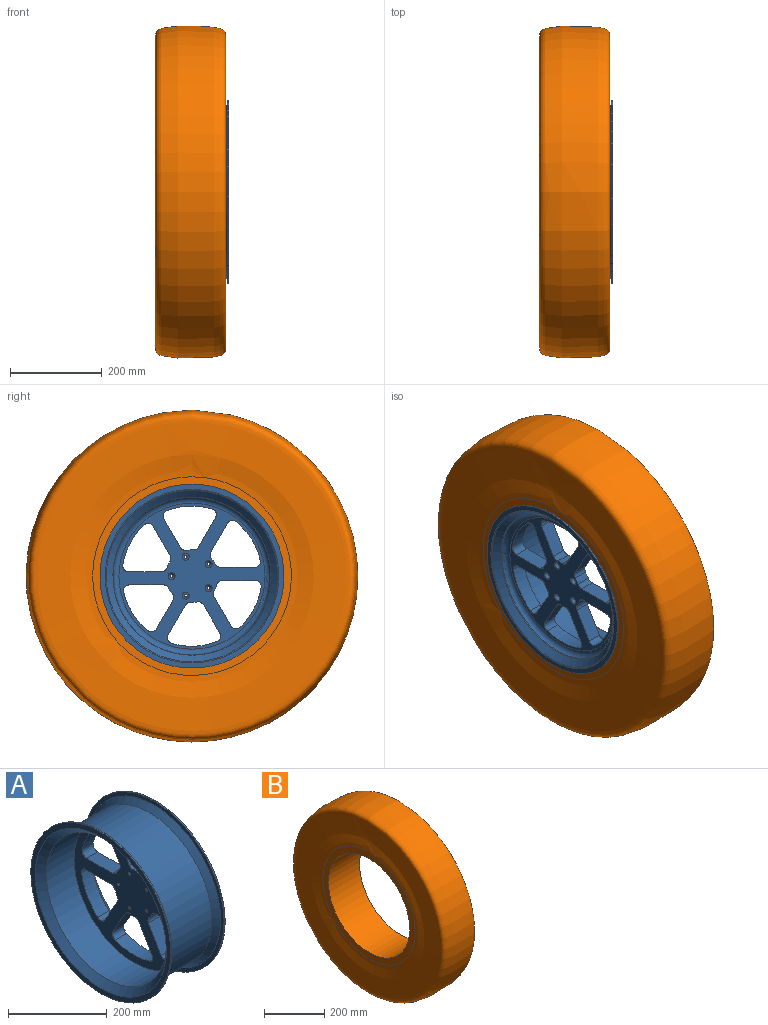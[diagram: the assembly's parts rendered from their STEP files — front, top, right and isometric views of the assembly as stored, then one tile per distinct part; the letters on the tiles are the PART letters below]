
ASSEMBLY  parts=2 mates=1
PART A: 80 faces, bbox 155.6x413.2x413.2 mm
  f0: plane 342.9x342.9mm, normal (-1,0,0), area 46675.4mm2, adj f7,f17,f18,f19,f20,f21,f22,f23
  f1: plane 317.61x317.61mm, normal (1,0,0), area 32801.7mm2, adj f16,f17,f18,f19,f20,f21,f22,f23
  f2: cone r=177.8mm half-angle=45deg, axis (-1,0,0), area 20781.2mm2, adj f3,f13
  f3: plane 400.05x400.05mm, normal (1,0,0), area 11685.9mm2, adj f2,f4
  f4: cylinder r=200.03mm len=400.05mm, axis (1,0,0), area 3990.3mm2, adj f3,f5
  f5: plane 400.05x400.05mm, normal (-1,0,0), area 15454.6mm2, adj f4,f6
  f6: cone r=171.45mm half-angle=45deg, axis (-1,0,0), area 25304.7mm2, adj f5,f7
  f7: cylinder r=171.45mm len=342.9mm, axis (1,0,0), area 85506.9mm2, adj f0,f6
  f8: cone r=187.32mm half-angle=45deg, axis (1,0,0), area 22340mm2, adj f14,f15
  f9: plane 400.05x400.05mm, normal (1,0,0), area 13901.2mm2, adj f10,f15
  f10: cylinder r=200.03mm len=400.05mm, axis (1,0,0), area 3990.3mm2, adj f9,f11
  f11: plane 400.05x400.05mm, normal (-1,0,0), area 11685.9mm2, adj f10,f12
  f12: cone r=177.8mm half-angle=45deg, axis (1,0,0), area 20781.2mm2, adj f11,f13
  f13: cylinder r=177.8mm len=355.6mm, axis (1,0,0), area 138331.1mm2, adj f2,f12
  f14: torus R=174.62mm, axis (-1,0,0), area 2407.6mm2, adj f8,f16
  f15: torus R=188.64mm, axis (-1,0,0), area 2937.1mm2, adj f8,f9
  f16: torus R=158.8mm, axis (-1,0,0), area 19783.7mm2, adj f1,f14
  f17: plane 62.09x35.85mm, normal (0,0.87,-0.5), area 2276.5mm2, adj f0,f1,f21,f24
  f18: cylinder r=57.15mm len=31.75mm, axis (1,0,0), area 456.4mm2, adj f0,f1,f21,f22
  f19: plane 73.83x31.75mm, normal (0,0,1), area 2344mm2, adj f0,f1,f22,f23
  f20: cylinder r=152.4mm len=83.54mm, axis (1,0,0), area 3184.6mm2, adj f0,f1,f23,f24
  f21: cylinder r=12.7mm len=31.75mm, axis (1,0,0), area 502.8mm2, adj f0,f1,f17,f18
  f22: cylinder r=12.7mm len=31.75mm, axis (1,0,0), area 443.1mm2, adj f0,f1,f18,f19
  f23: cylinder r=12.7mm len=31.75mm, axis (1,0,0), area 725.8mm2, adj f0,f1,f19,f20
  f24: cylinder r=12.7mm len=31.75mm, axis (1,0,0), area 697.8mm2, adj f0,f1,f17,f20
  f25: plane 71.7x31.75mm, normal (0,0,-1), area 2276.5mm2, adj f0,f1,f29,f32
  f26: cylinder r=57.15mm len=31.75mm, axis (1,0,0), area 456.4mm2, adj f0,f1,f29,f30
  f27: plane 63.94x36.91mm, normal (0,0.87,0.5), area 2344mm2, adj f0,f1,f30,f31
  f28: cylinder r=152.4mm len=86.97mm, axis (1,0,0), area 3184.6mm2, adj f0,f1,f31,f32
  f29: cylinder r=12.7mm len=31.75mm, axis (1,0,0), area 502.8mm2, adj f0,f1,f25,f26
  f30: cylinder r=12.7mm len=31.75mm, axis (1,0,0), area 443.1mm2, adj f0,f1,f26,f27
  f31: cylinder r=12.7mm len=31.75mm, axis (1,0,0), area 725.8mm2, adj f0,f1,f27,f28
  f32: cylinder r=12.7mm len=31.75mm, axis (1,0,0), area 697.8mm2, adj f0,f1,f25,f28
  f33: plane 62.09x35.85mm, normal (0,-0.87,-0.5), area 2276.5mm2, adj f0,f1,f37,f40
  f34: cylinder r=57.15mm len=31.75mm, axis (1,0,0), area 456.4mm2, adj f0,f1,f37,f38
  f35: plane 63.94x36.91mm, normal (0,0.87,-0.5), area 2344mm2, adj f0,f1,f38,f39
  f36: cylinder r=152.4mm len=98.44mm, axis (1,0,0), area 3184.6mm2, adj f0,f1,f39,f40
  f37: cylinder r=12.7mm len=31.75mm, axis (1,0,0), area 502.8mm2, adj f0,f1,f33,f34
  f38: cylinder r=12.7mm len=31.75mm, axis (1,0,0), area 443.1mm2, adj f0,f1,f34,f35
  f39: cylinder r=12.7mm len=31.75mm, axis (1,0,0), area 725.8mm2, adj f0,f1,f35,f36
  f40: cylinder r=12.7mm len=31.75mm, axis (1,0,0), area 697.8mm2, adj f0,f1,f33,f36
  f41: plane 62.09x35.85mm, normal (0,-0.87,0.5), area 2276.5mm2, adj f0,f1,f45,f48
  f42: cylinder r=57.15mm len=31.75mm, axis (1,0,0), area 456.4mm2, adj f0,f1,f45,f46
  f43: plane 73.83x31.75mm, normal (0,0,-1), area 2344mm2, adj f0,f1,f46,f47
  f44: cylinder r=152.4mm len=83.54mm, axis (1,0,0), area 3184.6mm2, adj f0,f1,f47,f48
  f45: cylinder r=12.7mm len=31.75mm, axis (1,0,0), area 502.8mm2, adj f0,f1,f41,f42
  f46: cylinder r=12.7mm len=31.75mm, axis (1,0,0), area 443.1mm2, adj f0,f1,f42,f43
  f47: cylinder r=12.7mm len=31.75mm, axis (1,0,0), area 725.8mm2, adj f0,f1,f43,f44
  f48: cylinder r=12.7mm len=31.75mm, axis (1,0,0), area 697.8mm2, adj f0,f1,f41,f44
  f49: plane 71.7x31.75mm, normal (0,0,1), area 2276.5mm2, adj f0,f1,f53,f56
  f50: cylinder r=57.15mm len=31.75mm, axis (1,0,0), area 456.4mm2, adj f0,f1,f53,f54
  f51: plane 63.94x36.91mm, normal (0,-0.87,-0.5), area 2344mm2, adj f0,f1,f54,f55
  f52: cylinder r=152.4mm len=86.97mm, axis (1,0,0), area 3184.6mm2, adj f0,f1,f55,f56
  f53: cylinder r=12.7mm len=31.75mm, axis (1,0,0), area 502.8mm2, adj f0,f1,f49,f50
  f54: cylinder r=12.7mm len=31.75mm, axis (1,0,0), area 443.1mm2, adj f0,f1,f50,f51
  f55: cylinder r=12.7mm len=31.75mm, axis (1,0,0), area 725.8mm2, adj f0,f1,f51,f52
  f56: cylinder r=12.7mm len=31.75mm, axis (1,0,0), area 697.8mm2, adj f0,f1,f49,f52
  f57: plane 62.09x35.85mm, normal (0,0.87,0.5), area 2276.5mm2, adj f0,f1,f61,f64
  f58: cylinder r=57.15mm len=31.75mm, axis (1,0,0), area 456.4mm2, adj f0,f1,f61,f62
  f59: plane 63.94x36.91mm, normal (0,-0.87,0.5), area 2344mm2, adj f0,f1,f62,f63
  f60: cylinder r=152.4mm len=98.44mm, axis (1,0,0), area 3184.6mm2, adj f0,f1,f63,f64
  f61: cylinder r=12.7mm len=31.75mm, axis (1,0,0), area 502.8mm2, adj f0,f1,f57,f58
  f62: cylinder r=12.7mm len=31.75mm, axis (1,0,0), area 443.1mm2, adj f0,f1,f58,f59
  f63: cylinder r=12.7mm len=31.75mm, axis (1,0,0), area 725.8mm2, adj f0,f1,f59,f60
  f64: cylinder r=12.7mm len=31.75mm, axis (1,0,0), area 697.8mm2, adj f0,f1,f57,f60
  f65: cylinder r=3.17mm len=14.61mm, axis (-1,0,0), area 291.4mm2, adj f0,f67
  f66: cylinder r=7.62mm len=15.24mm, axis (-1,0,0), area 608mm2, adj f1,f67
  f67: cone r=7.62mm half-angle=45deg, axis (1,0,0), area 213.2mm2, adj f65,f66
  f68: cylinder r=3.17mm len=14.61mm, axis (-1,0,0), area 291.4mm2, adj f0,f70
  f69: cylinder r=7.62mm len=15.24mm, axis (-1,0,0), area 608mm2, adj f1,f70
  f70: cone r=7.62mm half-angle=45deg, axis (1,0,0), area 213.2mm2, adj f68,f69
  f71: cylinder r=3.17mm len=14.61mm, axis (-1,0,0), area 291.4mm2, adj f0,f73
  f72: cylinder r=7.62mm len=15.24mm, axis (-1,0,0), area 608mm2, adj f1,f73
  f73: cone r=7.62mm half-angle=45deg, axis (1,0,0), area 213.2mm2, adj f71,f72
  f74: cylinder r=3.17mm len=14.61mm, axis (-1,0,0), area 291.4mm2, adj f0,f76
  f75: cylinder r=7.62mm len=15.24mm, axis (-1,0,0), area 608mm2, adj f1,f76
  f76: cone r=7.62mm half-angle=45deg, axis (1,0,0), area 213.2mm2, adj f74,f75
  f77: cylinder r=3.17mm len=14.61mm, axis (-1,0,0), area 291.4mm2, adj f0,f79
  f78: cylinder r=7.62mm len=15.24mm, axis (-1,0,0), area 608mm2, adj f1,f79
  f79: cone r=7.62mm half-angle=45deg, axis (1,0,0), area 213.2mm2, adj f77,f78
PART B: 4 faces, bbox 153.5x722.7x722.7 mm
  f0: plane 431.8x431.8mm, normal (-1,0,0), area 32430.8mm2, adj f1,f3
  f1: cylinder r=190.5mm len=381mm, axis (1,0,0), area 174814.1mm2, adj f0,f2
  f2: plane 431.8x431.8mm, normal (1,0,0), area 32429.3mm2, adj f1,f3
  f3: revolved ~722.74x722.74mm, area 1633468.4mm2, adj f0,f2
PLACE A rot(axis=(0,1,0),180deg) t=(8.14,115.83,62.21)mm
PLACE B t=(128.79,115.83,62.21)mm
MATE fastened A.f34 <-> B.f1  axis (-1,0,0) through (20.84,115.83,62.21)mm
